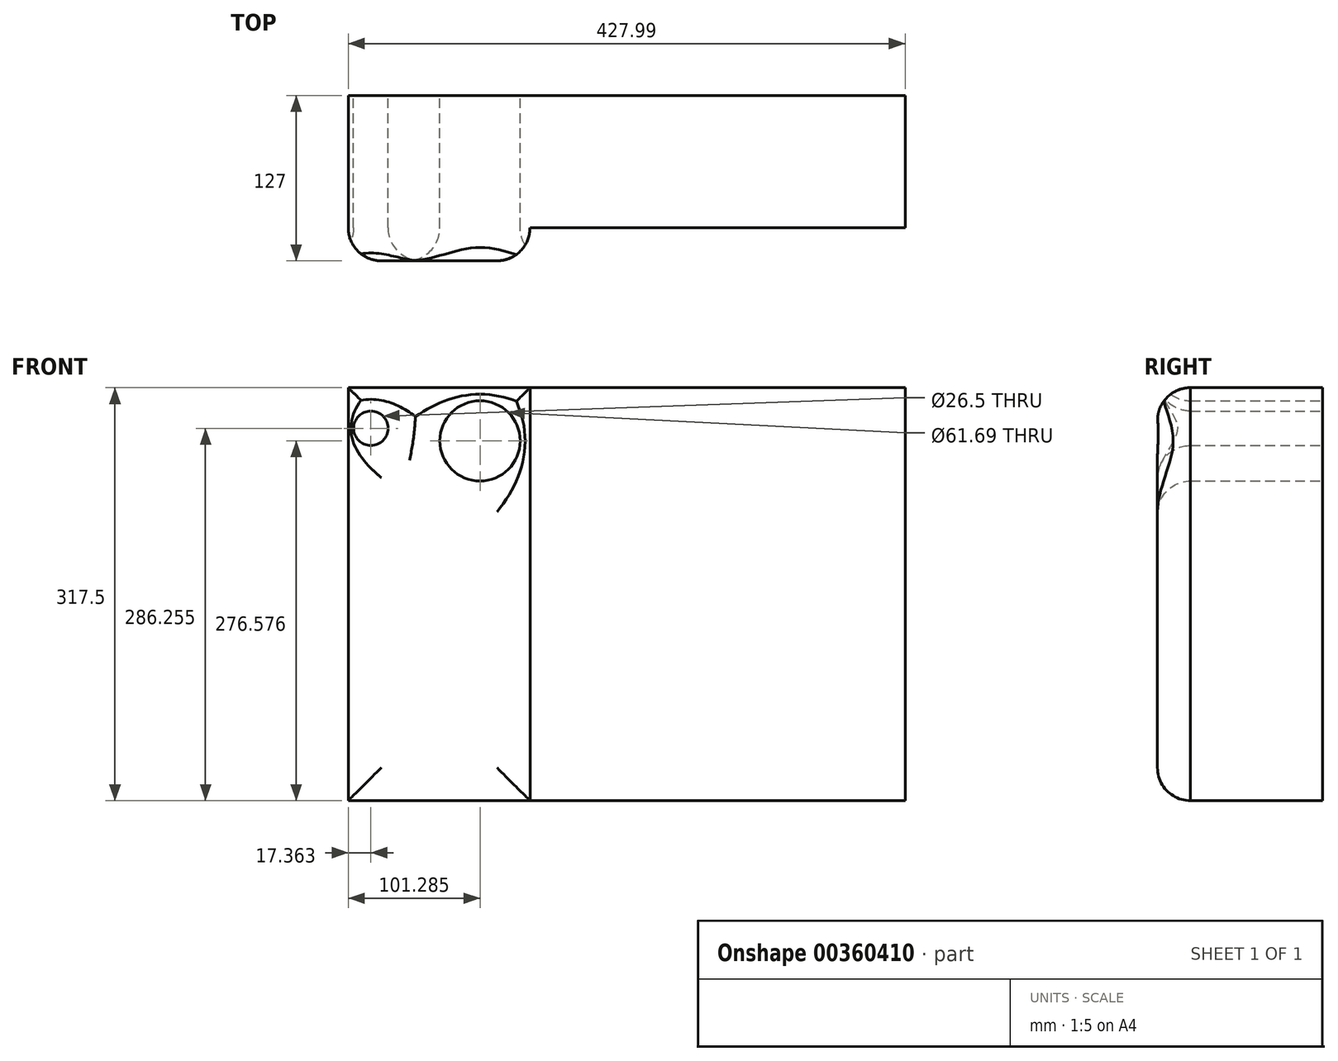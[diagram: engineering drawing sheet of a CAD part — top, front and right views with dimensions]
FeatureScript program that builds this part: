
annotation { "Feature Type Name" : "Feature", "Feature Type Description" : "" }
export const myFeature = defineFeature(function(context is Context, id is Id, definition is map)
    precondition{}
    {
        {
            var Q0;
            Q0=qCreatedBy(makeId("Front.planeOp"),FACE);
            var sketch = newSketch(context, id + "F0", { "sketchPlane" : qUnion([Q0])});
            skLineSegment(sketch, "E0.bottom", {"start": v(-51.8, 245.92) * mm, "end": v(87.9, 245.92) * mm});
            skLineSegment(sketch, "E0.top", {"start": v(-51.8, -71.58) * mm, "end": v(87.9, -71.58) * mm});
            skLineSegment(sketch, "E0.left", {"start": v(-51.8, 245.92) * mm, "end": v(-51.8, -71.58) * mm});
            skLineSegment(sketch, "E0.right", {"start": v(87.9, 245.92) * mm, "end": v(87.9, -71.58) * mm});
            skCircle(sketch, "E1", {"center": v(-34.45, 214.67) * mm, "radius": 13.25 * mm});
            skCircle(sketch, "E2", {"center": v(49.48, 205) * mm, "radius": 30.85 * mm});
            skSolve(sketch);
        }
        {
            var Q0;
            Q0=makeQuery(id+"F0.imprint","IMPRINT",FACE,{"disambiguationData":[TD([[makeQuery(id+"F0.imprint","IMPRINT",EDGE,{"derivedFrom":sQuery(id+"F0.wireOp",EDGE,"E0.bottom")}),-1.0]])]});
            extrude(context, id + "F1", {"entities" : qUnion([Q0]), "depth" : 127 * mm});
        }
        {
            var Q0;
            Q0=makeQuery(id+"F1.opExtrude","CAP_FACE",FACE,{"disambiguationData":[OSD([sQuery(id+"F0.wireOp",EDGE,"E0.bottom"),sQuery(id+"F0.wireOp",EDGE,"E0.top"),sQuery(id+"F0.wireOp",EDGE,"E0.left"),sQuery(id+"F0.wireOp",EDGE,"E0.right"),sQuery(id+"F0.wireOp",EDGE,"E1"),sQuery(id+"F0.wireOp",EDGE,"E2")])],"isStart":false});
            fillet(context, id + "F2", {"entities" : qUnion([Q0]), "radius" : 25.4 * mm, "tangentPropagation" : true, "allowEdgeOverflow" : false});
        }
        {
            var Q0;
            Q0=makeQuery(id+"F1.opExtrude","SWEPT_FACE",FACE,{"disambiguationData":[OSD([sQuery(id+"F0.wireOp",EDGE,"E0.right")])]});
            extrude(context, id + "F3", {"entities" : qUnion([Q0]), "operationType" : NewBodyOperationType.ADD, "depth" : 288.3 * mm});
        }
    });
